# Revit family: KEUCO_34908014411
name_source: partatom
category: Allgemeines Modell
revit_build: Autodesk Revit 2016 (Build: 20150220_1215(x64)
units: mm (PartAtom-declared; Revit-internal decimal feet)

## family parameters
Arbeitsebenenbasiert = Ja
Beim Laden mit Abzugskörper schneiden = Nein
Bemaßung runder Anschluss = Durchmesser verwenden
Gemeinsam genutzt = Nein
Immer vertikal = Nein
Kann Basisbauteil für Bewehrung sein = Nein
Raumberechnungspunkt = Nein
Teiletyp = Normal

## types (8) — shared parameters
Beschreibung = rechts und links verwendbar
komplett mit Brauseschieber
Hersteller = KEUCO
Material Stange = 1222 mm  [stored 4.00919 ft]
Serie = Plan
URL = https://www.keuco.com
Verbindung = 80 mm  [stored 0.262467 ft]
Verwendung = CA / DU
Vorgabe-Ansicht = 1219 mm
zero-valued in all types: Gewicht

## per-type parameters (varying)
| type | Ausschreibungstext | Stange A Länge  | Stange B Länge | Stange Material |
| 34908014411 | KEUCO PLAN CARE Duschhandlauf mit Brausestange 34908014411, 
hochglanzverchromter Duschhandlauf, komplett mit Brausehalter, 
in ästhetischem, funktionalem und ergonomischem Design,
Ausführung rechts und links verwendbar, 
speziell für den Dusch- und Wannenbereich 
als Hilfe zum Festhalten und Abstützen,
bis 115 kg belastbar, antistatisch, leicht zu reinigen,
Achsmaß waagerecht 400/400 mm, senkrecht 1182 mm,
Rohrdurchmesser 33 mm, 5 Rosetten Durchmesser 82 mm,
Außenmaße 579 mm, 680 mm, 1265 mm,
Ausladung 90 mm, Wandabstand 57 mm,
Der Duschhandlauf wird verdeckt angebracht

Im Lieferumfang enthalten: 
5 x Befestigungs-Set 1 
Art.-Nr. 34990000100 (je 1 x pro Wandbefestigung) 

Der Handlauf ist Bauart geprüft

Der Griff ist kombinierbar mit dem Duschspritzschutz 34940 
und dem Klappsitz mit Rückenlehne 34981

Weitere Befestigungs-Sets
(je nach Ankergrund/Mauerwerk):
5 x Befestigungs-Set 4 (Art.-Nr. 34990000200) oder
5 x Befestigungs-Set 7 (Art.-Nr. 34993000200) | 560 mm  [stored 1.83727 ft] | 796 mm  [stored 2.61155 ft] | Verchromt |
| 34908014611 | KEUCO PLAN CARE Duschhandlauf mit Brausestange 34908014611 
hochglanzverchromter Duschhandlauf, komplett mit Brausehalter, 
in ästhetischem, funktionalem und ergonomischem Design,
Ausführung rechts und links verwendbar, 
speziell für den Dusch- und Wannenbereich 
als Hilfe zum Festhalten und Abstützen,
bis 115 kg belastbar, antistatisch, leicht zu reinigen,
Achsmaß waagerecht 400/600 mm, senkrecht 1182 mm,
Rohrdurchmesser 33 mm, 5 Rosetten Durchmesser 82 mm,
Außenmaße 579 mm, 880 mm, 1265 mm,
Ausladung 90 mm, Wandabstand 57 mm,
Der Duschhandlauf wird verdeckt angebracht

Im Lieferumfang enthalten: 
5 x Befestigungs-Set 1 
Art.-Nr. 34990000100 (je 1 x pro Wandbefestigung) 

Der Handlauf ist Bauart geprüft

Der Griff ist kombinierbar mit dem Duschspritzschutz 34940 
und dem Klappsitz mit Rückenlehne 34981

Weitere Befestigungs-Sets
(je nach Ankergrund/Mauerwerk):
5 x Befestigungs-Set 4 (Art.-Nr. 34990000200) oder
5 x Befestigungs-Set 7 (Art.-Nr. 34993000200) | 560 mm  [stored 1.83727 ft] | 896 mm  [stored 2.93963 ft] | Verchromt |
| 34908016411 | KEUCO PLAN CARE Duschhandlauf mit Brausestange 34908016411 
hochglanzverchromter Duschhandlauf, komplett mit Brausehalter, 
in ästhetischem, funktionalem und ergonomischem Design,
Ausführung rechts und links verwendbar, 
speziell für den Dusch- und Wannenbereich 
als Hilfe zum Festhalten und Abstützen,
bis 115 kg belastbar, antistatisch, leicht zu reinigen,
Achsmaß waagerecht 600/400 mm, senkrecht 1182 mm,
Rohrdurchmesser 33 mm, 5 Rosetten Durchmesser 82 mm,
Außenmaße 779 mm, 680 mm, 1265 mm,
Ausladung 90 mm, Wandabstand 57 mm,
Der Duschhandlauf wird verdeckt angebracht

Im Lieferumfang enthalten: 
5 x Befestigungs-Set 1 
Art.-Nr. 34990000100 (je 1 x pro Wandbefestigung) 

Der Handlauf ist Bauart geprüft

Der Griff ist kombinierbar mit dem Duschspritzschutz 34940 
und dem Klappsitz mit Rückenlehne 34981

Weitere Befestigungs-Sets
(je nach Ankergrund/Mauerwerk):
5 x Befestigungs-Set 4 (Art.-Nr. 34990000200) oder
5 x Befestigungs-Set 7 (Art.-Nr. 34993000200) | 760 mm | 696 mm  [stored 2.28346 ft] | Verchromt |
| 34908016611 | KEUCO PLAN CARE Duschhandlauf mit Brausestange 34908016611 
hochglanzverchromter Duschhandlauf, komplett mit Brausehalter, 
in ästhetischem, funktionalem und ergonomischem Design,
Ausführung rechts und links verwendbar, 
speziell für den Dusch- und Wannenbereich 
als Hilfe zum Festhalten und Abstützen,
bis 115 kg belastbar, antistatisch, leicht zu reinigen,
Achsmaß waagerecht 600/600 mm, senkrecht 1182 mm,
Rohrdurchmesser 33 mm, 5 Rosetten Durchmesser 82 mm,
Außenmaße 797 mm, 880 mm, 1265 mm,
Ausladung 90 mm, Wandabstand 57 mm,
Der Duschhandlauf wird verdeckt angebracht

Im Lieferumfang enthalten: 
5 x Befestigungs-Set 1 
Art.-Nr. 34990000100 (je 1 x pro Wandbefestigung) 

Der Handlauf ist Bauart geprüft

Der Griff ist kombinierbar mit dem Duschspritzschutz 34940 
und dem Klappsitz mit Rückenlehne 34981

Weitere Befestigungs-Sets
(je nach Ankergrund/Mauerwerk):
5 x Befestigungs-Set 4 (Art.-Nr. 34990000200) oder
5 x Befestigungs-Set 7 (Art.-Nr. 34993000200) | 760 mm | 696 mm  [stored 2.28346 ft] | Verchromt |
| 34908174411 | KEUCO PLAN CARE Duschhandlauf mit Brausestange 34908174411 
Duschhandlauf Aluminium silber-eloxiert (E6 EV1)/verchromt, 
komplett mit Brausehalter, 
in ästhetischem, funktionalem und ergonomischem Design,
Ausführung rechts und links verwendbar, 
speziell für den Dusch- und Wannenbereich 
als Hilfe zum Festhalten und Abstützen,
bis 115 kg belastbar, antistatisch, leicht zu reinigen,
Achsmaß waagerecht 400/400 mm, senkrecht 1182 mm,
Rohrdurchmesser 33 mm, 5 Rosetten Durchmesser 82 mm,
Außenmaße 579 mm, 680 mm, 1265 mm,
Ausladung 90 mm, Wandabstand 57 mm,
Der Duschhandlauf wird verdeckt angebracht

Im Lieferumfang enthalten: 
5 x Befestigungs-Set 1 
Art.-Nr. 34990000100 (je 1 x pro Wandbefestigung) 

Der Handlauf ist Bauart geprüft

Der Griff ist kombinierbar mit dem Duschspritzschutz 34940 
und dem Klappsitz mit Rückenlehne 34981

Weitere Befestigungs-Sets
(je nach Ankergrund/Mauerwerk):
5 x Befestigungs-Set 4 (Art.-Nr. 34990000200) oder
5 x Befestigungs-Set 7 (Art.-Nr. 34993000200) | 560 mm  [stored 1.83727 ft] | 796 mm  [stored 2.61155 ft] | Aluminium silber-eloxiert (E6 EV1) |
| 34908174611 | KEUCO PLAN CARE Duschhandlauf mit Brausestange 34908174611 
Duschhandlauf Aluminium silber-eloxiert (E6 EV1)/verchromt, 
komplett mit Brausehalter, 
in ästhetischem, funktionalem und ergonomischem Design,
Ausführung rechts und links verwendbar, 
speziell für den Dusch- und Wannenbereich 
als Hilfe zum Festhalten und Abstützen,
bis 115 kg belastbar, antistatisch, leicht zu reinigen,
Achsmaß waagerecht 400/600 mm, senkrecht 1182 mm,
Rohrdurchmesser 33 mm, 5 Rosetten Durchmesser 82 mm,
Außenmaße 579 mm, 880 mm, 1265 mm,
Ausladung 90 mm, Wandabstand 57 mm,
Der Duschhandlauf wird verdeckt angebracht

Im Lieferumfang enthalten: 
5 x Befestigungs-Set 1 
Art.-Nr. 34990000100 (je 1 x pro Wandbefestigung) 

Der Handlauf ist Bauart geprüft

Der Griff ist kombinierbar mit dem Duschspritzschutz 34940 
und dem Klappsitz mit Rückenlehne 34981

Weitere Befestigungs-Sets
(je nach Ankergrund/Mauerwerk):
5 x Befestigungs-Set 4 (Art.-Nr. 34990000200) oder
5 x Befestigungs-Set 7 (Art.-Nr. 34993000200) | 560 mm  [stored 1.83727 ft] | 896 mm  [stored 2.93963 ft] | Verchromt |
| 34908176411 | KEUCO PLAN CARE Duschhandlauf mit Brausestange 34908176411 
Duschhandlauf Aluminium silber-eloxiert (E6 EV1)/verchromt, 
komplett mit Brausehalter, 
in ästhetischem, funktionalem und ergonomischem Design,
Ausführung rechts und links verwendbar, 
speziell für den Dusch- und Wannenbereich 
als Hilfe zum Festhalten und Abstützen,
bis 115 kg belastbar, antistatisch, leicht zu reinigen,
Achsmaß waagerecht 600/400 mm, senkrecht 1182 mm,
Rohrdurchmesser 33 mm, 5 Rosetten Durchmesser 82 mm,
Außenmaße 779 mm, 680 mm, 1265 mm,
Ausladung 90 mm, Wandabstand 57 mm,
Der Duschhandlauf wird verdeckt angebracht

Im Lieferumfang enthalten: 
5 x Befestigungs-Set 1 
Art.-Nr. 34990000100 (je 1 x pro Wandbefestigung) 

Der Handlauf ist Bauart geprüft

Der Griff ist kombinierbar mit dem Duschspritzschutz 34940 
und dem Klappsitz mit Rückenlehne 34981

Weitere Befestigungs-Sets
(je nach Ankergrund/Mauerwerk):
5 x Befestigungs-Set 4 (Art.-Nr. 34990000200) oder
5 x Befestigungs-Set 7 (Art.-Nr. 34993000200) | 760 mm | 696 mm  [stored 2.28346 ft] | Aluminium silber-eloxiert (E6 EV1) |
| 34908176611 | KEUCO PLAN CARE Duschhandlauf mit Brausestange 34908176611 
Duschhandlauf Aluminium silber-eloxiert (E6 EV1)/verchromt, 
komplett mit Brausehalter, 
in ästhetischem, funktionalem und ergonomischem Design,
Ausführung rechts und links verwendbar, 
speziell für den Dusch- und Wannenbereich 
als Hilfe zum Festhalten und Abstützen,
bis 115 kg belastbar, antistatisch, leicht zu reinigen,
Achsmaß waagerecht 600/600 mm, senkrecht 1182 mm,
Rohrdurchmesser 33 mm, 5 Rosetten Durchmesser 82 mm,
Außenmaße 797 mm, 880 mm, 1265 mm,
Ausladung 90 mm, Wandabstand 57 mm,
Der Duschhandlauf wird verdeckt angebracht

Im Lieferumfang enthalten: 
5 x Befestigungs-Set 1 
Art.-Nr. 34990000100 (je 1 x pro Wandbefestigung) 

Der Handlauf ist Bauart geprüft

Der Griff ist kombinierbar mit dem Duschspritzschutz 34940 
und dem Klappsitz mit Rückenlehne 34981

Weitere Befestigungs-Sets
(je nach Ankergrund/Mauerwerk):
5 x Befestigungs-Set 4 (Art.-Nr. 34990000200) oder
5 x Befestigungs-Set 7 (Art.-Nr. 34993000200) | 660 mm | 896 mm  [stored 2.93963 ft] | Aluminium silber-eloxiert (E6 EV1) |

note: column(s) folded — value = type name in every type: Artikelnummer

note: [stored X ft] marks values corroborated as IEEE doubles in the binary element streams (Revit-internal decimal feet)

## geometry (parser evidence)
native form markers: Sweep x1
no freeform markers — native parametric forms only
